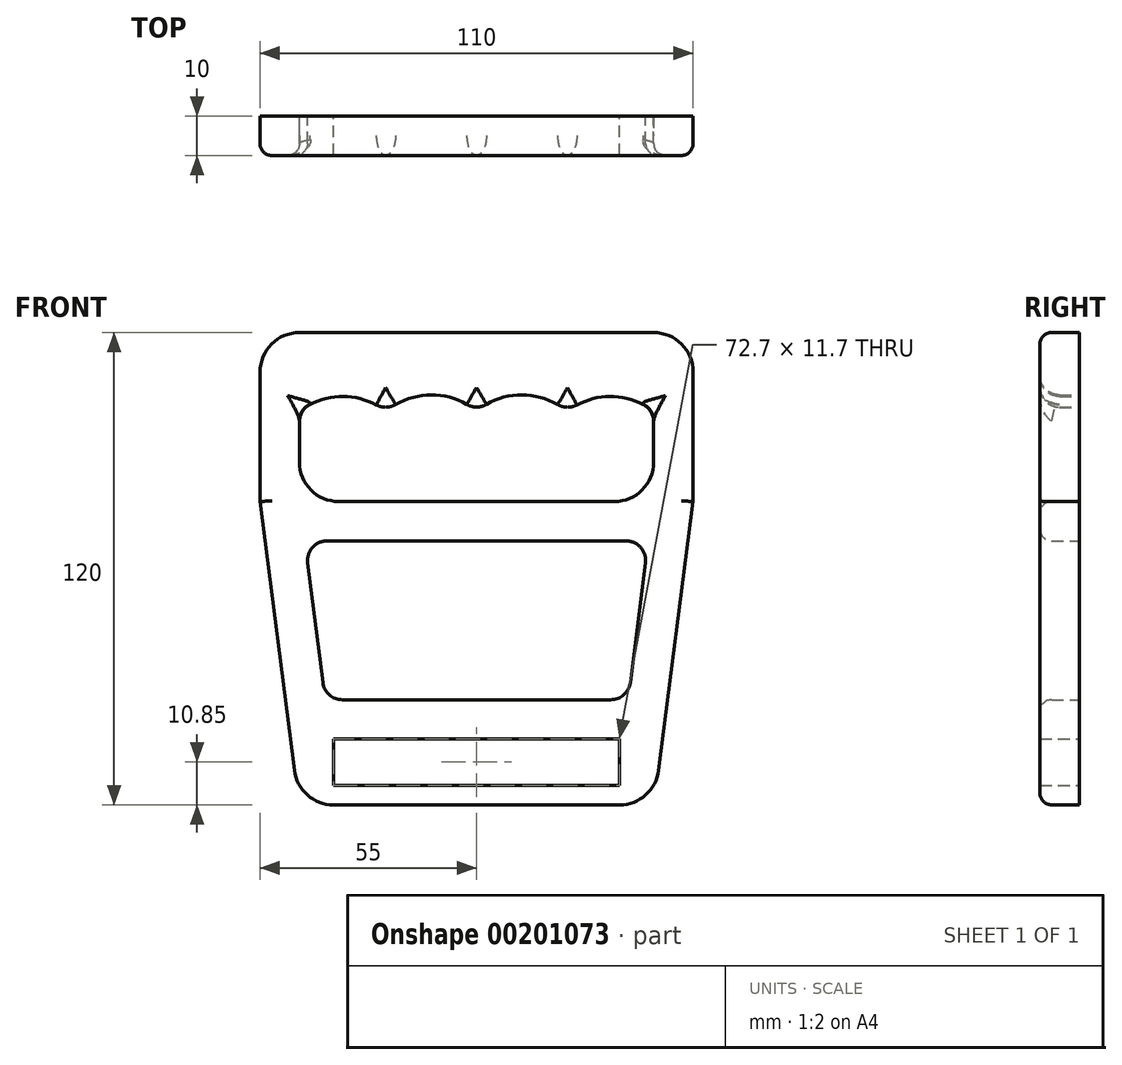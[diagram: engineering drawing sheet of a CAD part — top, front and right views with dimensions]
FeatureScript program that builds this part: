
annotation { "Feature Type Name" : "Feature", "Feature Type Description" : "" }
export const myFeature = defineFeature(function(context is Context, id is Id, definition is map)
    precondition{}
    {
        {
            var Q0;
            Q0=qCreatedBy(makeId("Front.planeOp"),FACE);
            var sketch = newSketch(context, id + "F0", { "sketchPlane" : qUnion([Q0])});
            skLineSegment(sketch, "E0.bottom", {"start": v(36.35, 5.85) * mm, "end": v(-36.35, 5.85) * mm});
            skLineSegment(sketch, "E0.top", {"start": v(36.35, -5.85) * mm, "end": v(-36.35, -5.85) * mm});
            skLineSegment(sketch, "E0.left", {"start": v(36.35, 5.85) * mm, "end": v(36.35, -5.85) * mm});
            skLineSegment(sketch, "E0.right", {"start": v(-36.35, 5.85) * mm, "end": v(-36.35, -5.85) * mm});
            skPoint(sketch, "E0.middle", {"position": v(0, 0) * mm});
            skLineSegment(sketch, "E1.bottom", {"start": v(-36.35, -10.85) * mm, "end": v(36.35, -10.85) * mm});
            skLineSegment(sketch, "E1.top", {"start": v(-45, 109.15) * mm, "end": v(45, 109.15) * mm});
            skLineSegment(sketch, "E1.left", {"start": v(-55, 66.22) * mm, "end": v(-55, 99.15) * mm});
            skLineSegment(sketch, "E1.right", {"start": v(55, 66.22) * mm, "end": v(55, 99.15) * mm});
            skPoint(sketch, "E2.middle", {"position": v(0, 36.03) * mm});
            skLineSegment(sketch, "E3.bottom", {"start": v(35, 66.22) * mm, "end": v(-35, 66.22) * mm});
            skLineSegment(sketch, "E3.left", {"start": v(45, 76.22) * mm, "end": v(45, 89.15) * mm});
            skLineSegment(sketch, "E3.right", {"start": v(-45, 76.22) * mm, "end": v(-45, 89.15) * mm});
            skPoint(sketch, "E3.middle", {"position": v(0, 77.68) * mm});
            skPoint(sketch, "E4.visualSharp", {"position": v(-55, 109.15) * mm});
            skArc(sketch, "E4.filletArc", {"start": v(-45, 109.15) * mm, "mid": v(-52.07, 106.22) * mm, "end": v(-55, 99.15) * mm});
            skPoint(sketch, "E5.visualSharp", {"position": v(55, 109.15) * mm});
            skArc(sketch, "E5.filletArc", {"start": v(55, 99.15) * mm, "mid": v(52.07, 106.22) * mm, "end": v(45, 109.15) * mm});
            skPoint(sketch, "E6.visualSharp", {"position": v(-55, -10.85) * mm});
            skPoint(sketch, "E7.visualSharp", {"position": v(55, -10.85) * mm});
            skPoint(sketch, "E8.visualSharp", {"position": v(-45, 66.22) * mm});
            skArc(sketch, "E8.filletArc", {"start": v(-45, 76.22) * mm, "mid": v(-42.07, 69.15) * mm, "end": v(-35, 66.22) * mm});
            skPoint(sketch, "E9.visualSharp", {"position": v(45, 66.22) * mm});
            skArc(sketch, "E9.filletArc", {"start": v(35, 66.22) * mm, "mid": v(42.07, 69.15) * mm, "end": v(45, 76.22) * mm});
            skPoint(sketch, "E10.visualSharp", {"position": v(45, 56.22) * mm});
            skPoint(sketch, "E11.visualSharp", {"position": v(45, 15.85) * mm});
            skPoint(sketch, "E12.visualSharp", {"position": v(-45, 56.22) * mm});
            skPoint(sketch, "E13.visualSharp", {"position": v(-45, 15.85) * mm});
            skArc(sketch, "E14", {"start": v(-23, 89.15) * mm, "mid": v(-34, 92.9) * mm, "end": v(-45, 89.15) * mm});
            skArc(sketch, "E15", {"start": v(0, 89.15) * mm, "mid": v(-11.5, 93.3) * mm, "end": v(-23, 89.15) * mm});
            skArc(sketch, "E16", {"start": v(23, 89.15) * mm, "mid": v(11.5, 93.3) * mm, "end": v(0, 89.15) * mm});
            skArc(sketch, "E17", {"start": v(45, 89.15) * mm, "mid": v(34, 92.9) * mm, "end": v(23, 89.15) * mm});
            skLineSegment(sketch, "E18", {"start": v(-46.27, -2.12) * mm, "end": v(-55, 66.22) * mm});
            skLineSegment(sketch, "E19", {"start": v(46.27, -2.12) * mm, "end": v(55, 66.22) * mm});
            skPoint(sketch, "E20.visualSharp", {"position": v(-45.15, -10.85) * mm});
            skArc(sketch, "E20.filletArc", {"start": v(-46.27, -2.12) * mm, "mid": v(-42.96, -8.36) * mm, "end": v(-36.35, -10.85) * mm});
            skPoint(sketch, "E21.visualSharp", {"position": v(45.15, -10.85) * mm});
            skArc(sketch, "E21.filletArc", {"start": v(36.35, -10.85) * mm, "mid": v(42.96, -8.36) * mm, "end": v(46.27, -2.12) * mm});
            skLineSegment(sketch, "E22", {"start": v(-42.92, 50.58) * mm, "end": v(-39.04, 20.22) * mm});
            skLineSegment(sketch, "E23", {"start": v(-34.08, 15.85) * mm, "end": v(34.08, 15.85) * mm});
            skLineSegment(sketch, "E24", {"start": v(39.04, 20.22) * mm, "end": v(42.92, 50.58) * mm});
            skLineSegment(sketch, "E25", {"start": v(37.96, 56.22) * mm, "end": v(-37.96, 56.22) * mm});
            skPoint(sketch, "E26.visualSharp", {"position": v(-43.64, 56.22) * mm});
            skArc(sketch, "E26.filletArc", {"start": v(-37.96, 56.22) * mm, "mid": v(-41.71, 54.52) * mm, "end": v(-42.92, 50.58) * mm});
            skPoint(sketch, "E27.visualSharp", {"position": v(-38.48, 15.85) * mm});
            skArc(sketch, "E27.filletArc", {"start": v(-39.04, 20.22) * mm, "mid": v(-37.39, 17.1) * mm, "end": v(-34.08, 15.85) * mm});
            skPoint(sketch, "E28.visualSharp", {"position": v(38.48, 15.85) * mm});
            skArc(sketch, "E28.filletArc", {"start": v(34.08, 15.85) * mm, "mid": v(37.39, 17.1) * mm, "end": v(39.04, 20.22) * mm});
            skPoint(sketch, "E29.visualSharp", {"position": v(43.64, 56.22) * mm});
            skArc(sketch, "E29.filletArc", {"start": v(42.92, 50.58) * mm, "mid": v(41.71, 54.52) * mm, "end": v(37.96, 56.22) * mm});
            skSolve(sketch);
        }
        {
            var Q0;
            Q0=makeQuery(id+"F0.imprint","IMPRINT",FACE,{"disambiguationData":[TD([[makeQuery(id+"F0.imprint","IMPRINT",EDGE,{"derivedFrom":sQuery(id+"F0.wireOp",EDGE,"E0.bottom")}),-1.0]])]});
            extrude(context, id + "F1", {"entities" : qUnion([Q0]), "depth" : 10 * mm, "offsetDistance" : 25 * mm});
        }
        {
            var Q0;
            Q0=makeQuery(id+"F1.opExtrude","CAP_EDGE",EDGE,{"disambiguationData":[OSD([sQuery(id+"F0.wireOp",EDGE,"E1.left")])],"isStart":false});
            var Q1;
            Q1=makeQuery(id+"F1.opExtrude","CAP_EDGE",EDGE,{"disambiguationData":[OSD([sQuery(id+"F0.wireOp",EDGE,"E2.top")])],"isStart":false});
            var Q2;
            Q2=makeQuery(id+"F1.opExtrude","CAP_EDGE",EDGE,{"disambiguationData":[OSD([sQuery(id+"F0.wireOp",EDGE,"E9.filletArc")])],"isStart":false});
            var Q3;
            Q3=makeQuery(id+"F1.opExtrude","CAP_EDGE",EDGE,{"disambiguationData":[OSD([sQuery(id+"F0.wireOp",EDGE,"E25")])],"isStart":false});
            var Q4;
            Q4=makeQuery(id+"F1.opExtrude","CAP_EDGE",EDGE,{"disambiguationData":[OSD([sQuery(id+"F0.wireOp",EDGE,"E19")])],"isStart":false});
            fillet(context, id + "F2", {"entities" : qUnion([Q0, Q1, Q2, Q3, Q4]), "radius" : 3 * mm, "tangentPropagation" : true, "allowEdgeOverflow" : false});
        }
        {
            var Q0;
            Q0=makeQuery(id+"F1.opExtrude","CAP_EDGE",EDGE,{"disambiguationData":[OSD([sQuery(id+"F0.wireOp",EDGE,"E14")])],"isStart":false});
            var Q1;
            Q1=makeQuery(id+"F1.opExtrude","CAP_EDGE",EDGE,{"disambiguationData":[OSD([sQuery(id+"F0.wireOp",EDGE,"E15")])],"isStart":false});
            var Q2;
            Q2=makeQuery(id+"F1.opExtrude","CAP_EDGE",EDGE,{"disambiguationData":[OSD([sQuery(id+"F0.wireOp",EDGE,"E16")])],"isStart":false});
            var Q3;
            Q3=makeQuery(id+"F1.opExtrude","CAP_EDGE",EDGE,{"disambiguationData":[OSD([sQuery(id+"F0.wireOp",EDGE,"E17")])],"isStart":false});
            fillet(context, id + "F3", {"entities" : qUnion([Q0, Q1, Q2, Q3]), "radius" : 5 * mm, "tangentPropagation" : true, "allowEdgeOverflow" : false});
        }
        {
            var Q0;
            Q0=makeQuery(id+"F3.opFillet","BLEND_EDGE",EDGE,{"blendedFrom":[makeQuery(id+"F1.opExtrude","CAP_EDGE",EDGE,{"disambiguationData":[OSD([sQuery(id+"F0.wireOp",EDGE,"E15")])],"isStart":false}),makeQuery(id+"F1.opExtrude","CAP_EDGE",EDGE,{"disambiguationData":[OSD([sQuery(id+"F0.wireOp",EDGE,"E14")])],"isStart":false})],"blendedInto":[]});
            var Q1;
            Q1=makeQuery(id+"F3.opFillet","BLEND_EDGE",EDGE,{"blendedFrom":[makeQuery(id+"F1.opExtrude","CAP_EDGE",EDGE,{"disambiguationData":[OSD([sQuery(id+"F0.wireOp",EDGE,"E15")])],"isStart":false}),makeQuery(id+"F1.opExtrude","CAP_EDGE",EDGE,{"disambiguationData":[OSD([sQuery(id+"F0.wireOp",EDGE,"E16")])],"isStart":false})],"blendedInto":[]});
            var Q2;
            Q2=makeQuery(id+"F3.opFillet","BLEND_EDGE",EDGE,{"blendedFrom":[makeQuery(id+"F1.opExtrude","CAP_EDGE",EDGE,{"disambiguationData":[OSD([sQuery(id+"F0.wireOp",EDGE,"E16")])],"isStart":false}),makeQuery(id+"F1.opExtrude","CAP_EDGE",EDGE,{"disambiguationData":[OSD([sQuery(id+"F0.wireOp",EDGE,"E17")])],"isStart":false})],"blendedInto":[]});
            var Q3;
            Q3=makeQuery(id+"F1.opExtrude","SWEPT_EDGE",EDGE,{"disambiguationData":[OSD([sQuery(id+"F0.wireOp",EDGE,"E3.left"),sQuery(id+"F0.wireOp",EDGE,"E17")])]});
            var Q4;
            Q4=makeQuery(id+"F1.opExtrude","SWEPT_EDGE",EDGE,{"disambiguationData":[OSD([sQuery(id+"F0.wireOp",EDGE,"E3.right"),sQuery(id+"F0.wireOp",EDGE,"E14")])]});
            fillet(context, id + "F4", {"entities" : qUnion([Q0, Q1, Q2, Q3, Q4]), "radius" : 5 * mm, "tangentPropagation" : true, "allowEdgeOverflow" : false});
        }
    });
